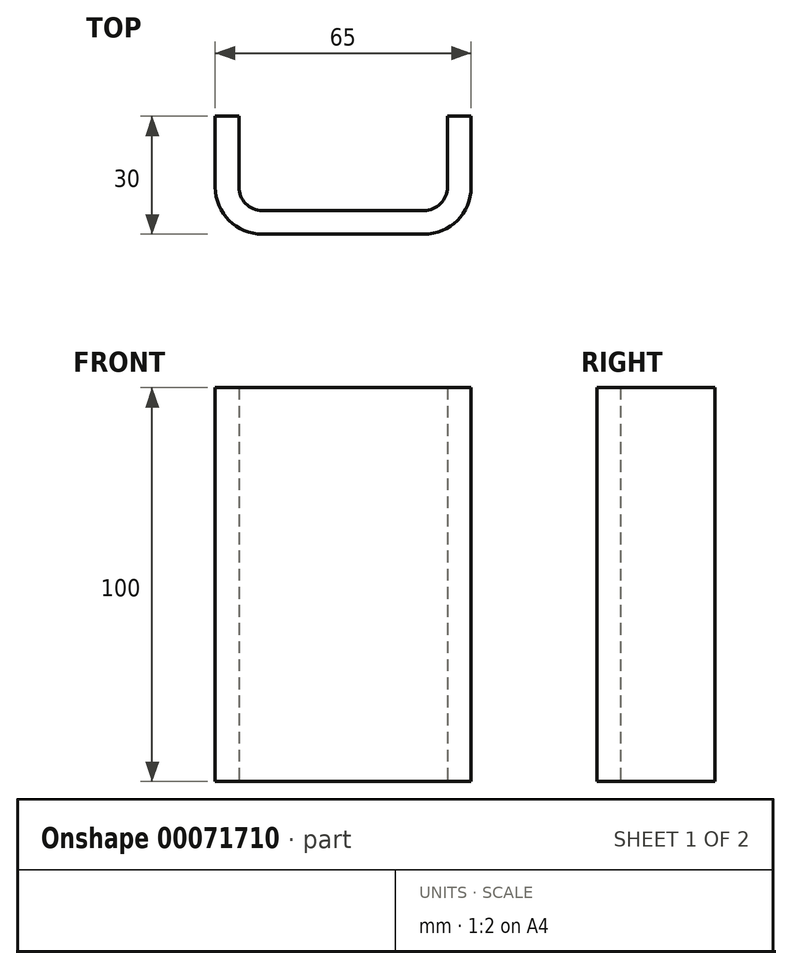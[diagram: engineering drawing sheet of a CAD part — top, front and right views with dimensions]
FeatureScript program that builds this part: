
annotation { "Feature Type Name" : "Feature", "Feature Type Description" : "" }
export const myFeature = defineFeature(function(context is Context, id is Id, definition is map)
    precondition{}
    {
        {
            var Q0;
            Q0=qCreatedBy(makeId("Top.planeOp"),FACE);
            var sketch = newSketch(context, id + "F0", { "sketchPlane" : qUnion([Q0])});
            skLineSegment(sketch, "E0", {"start": v(0, 0) * mm, "end": v(32.5, 0) * mm});
            skLineSegment(sketch, "E1", {"start": v(32.5, 0) * mm, "end": v(32.5, 30) * mm});
            skLineSegment(sketch, "E2.0", {"start": v(26.5, 6) * mm, "end": v(26.5, 30) * mm});
            skLineSegment(sketch, "E2.1", {"start": v(0, 6) * mm, "end": v(26.5, 6) * mm});
            skLineSegment(sketch, "E3", {"start": v(26.5, 30) * mm, "end": v(32.5, 30) * mm});
            skLineSegment(sketch, "E4", {"start": v(0, 0) * mm, "end": v(0, 20.85) * mm});
            skLineSegment(sketch, "E5.MirrorCS", {"start": v(-26.5, 6) * mm, "end": v(-26.5, 30) * mm});
            skLineSegment(sketch, "E6.MirrorCS", {"start": v(-26.5, 30) * mm, "end": v(-32.5, 30) * mm});
            skLineSegment(sketch, "E7.MirrorCS", {"start": v(-32.5, 0) * mm, "end": v(-32.5, 30) * mm});
            skLineSegment(sketch, "E8.MirrorCS", {"start": v(0, 6) * mm, "end": v(-26.5, 6) * mm});
            skLineSegment(sketch, "E9.MirrorCS", {"start": v(0, 0) * mm, "end": v(-32.5, 0) * mm});
            skSolve(sketch);
        }
        {
            var Q0;
            {var subQ1=sQuery(id+"F0.wireOp",EDGE,"E0");Q0=makeQuery(id+"F0.imprint","IMPRINT",FACE,{"disambiguationData":[TD([[makeQuery(id+"F0.imprint","IMPRINT",EDGE,{"derivedFrom":subQ1}),1.0]])]});}
            var Q1;
            Q1=makeQuery(id+"F0.imprint","IMPRINT",FACE,{"disambiguationData":[TD([[makeQuery(id+"F0.imprint","IMPRINT",EDGE,{"derivedFrom":sQuery(id+"F0.wireOp",EDGE,"E5.MirrorCS")}),1.0]])]});
            extrude(context, id + "F1", {"entities" : qUnion([Q0, Q1]), "depth" : 100 * mm});
        }
        {
            var Q0;
            Q0=makeQuery(id+"F1.opExtrude","SWEPT_EDGE",EDGE,{"disambiguationData":[OSD([sQuery(id+"F0.wireOp",EDGE,"E2.0"),sQuery(id+"F0.wireOp",EDGE,"E2.1")])]});
            var Q1;
            Q1=makeQuery(id+"F1.opExtrude","SWEPT_EDGE",EDGE,{"disambiguationData":[OSD([sQuery(id+"F0.wireOp",EDGE,"E5.MirrorCS"),sQuery(id+"F0.wireOp",EDGE,"E8.MirrorCS")])]});
            fillet(context, id + "F2", {"entities" : qUnion([Q0, Q1]), "radius" : 6 * mm, "tangentPropagation" : true, "allowEdgeOverflow" : false});
        }
        {
            var Q0;
            Q0=makeQuery(id+"F1.opExtrude","SWEPT_EDGE",EDGE,{"disambiguationData":[OSD([sQuery(id+"F0.wireOp",EDGE,"E0"),sQuery(id+"F0.wireOp",EDGE,"E1")])]});
            var Q1;
            Q1=makeQuery(id+"F1.opExtrude","SWEPT_EDGE",EDGE,{"disambiguationData":[OSD([sQuery(id+"F0.wireOp",EDGE,"E7.MirrorCS"),sQuery(id+"F0.wireOp",EDGE,"E9.MirrorCS")])]});
            fillet(context, id + "F3", {"entities" : qUnion([Q0, Q1]), "radius" : 12 * mm, "tangentPropagation" : true, "allowEdgeOverflow" : false});
        }
    });
